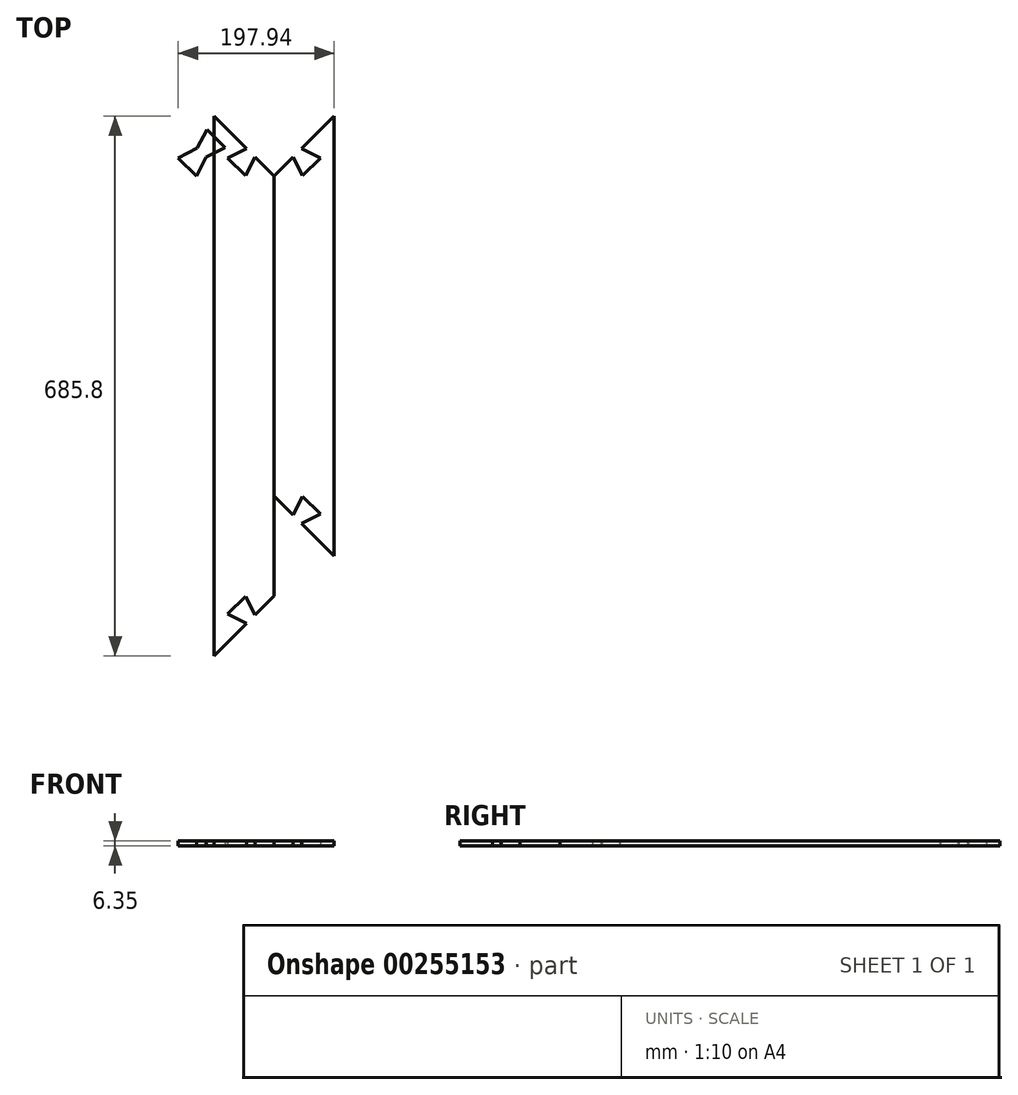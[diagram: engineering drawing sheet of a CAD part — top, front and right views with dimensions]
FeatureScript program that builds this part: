
annotation { "Feature Type Name" : "Feature", "Feature Type Description" : "" }
export const myFeature = defineFeature(function(context is Context, id is Id, definition is map)
    precondition{}
    {
        {
            assignVariable(context, id + "F0", {"name" : "BorderWidth", "anyValue" : 50});
        }
        {
            assignVariable(context, id + "F1", {"name" : "MaterialThickness", "anyValue" : 6.35});
        }
        {
            var Q0;
            Q0=qCreatedBy(makeId("Top.planeOp"),FACE);
            var sketch = newSketch(context, id + "F2", { "sketchPlane" : qUnion([Q0])});
            skLineSegment(sketch, "E0.bottom", {"start": v(203.2, 266.7) * mm, "end": v(-203.2, 266.7) * mm});
            skLineSegment(sketch, "E0.top", {"start": v(203.2, -266.7) * mm, "end": v(-203.2, -266.7) * mm});
            skLineSegment(sketch, "E0.left", {"start": v(203.2, 266.7) * mm, "end": v(203.2, -266.7) * mm});
            skLineSegment(sketch, "E0.right", {"start": v(-203.2, 266.7) * mm, "end": v(-203.2, -266.7) * mm});
            skPoint(sketch, "E0.middle", {"position": v(0, 0) * mm});
            skLineSegment(sketch, "E1.0", {"start": v(-279.4, 342.9) * mm, "end": v(-279.4, -342.9) * mm});
            skLineSegment(sketch, "E1.1", {"start": v(279.4, 342.9) * mm, "end": v(-279.4, 342.9) * mm});
            skLineSegment(sketch, "E1.2", {"start": v(279.4, 342.9) * mm, "end": v(279.4, -342.9) * mm});
            skLineSegment(sketch, "E1.3", {"start": v(279.4, -342.9) * mm, "end": v(-279.4, -342.9) * mm});
            skLineSegment(sketch, "E2", {"start": v(-203.2, 266.7) * mm, "end": v(-279.4, 342.9) * mm});
            skLineSegment(sketch, "E3", {"start": v(-238.22, 301.72) * mm, "end": v(-262.02, 289.6) * mm});
            skLineSegment(sketch, "E4", {"start": v(-262.02, 289.6) * mm, "end": v(-239.57, 267.15) * mm});
            skLineSegment(sketch, "E5", {"start": v(-239.57, 267.15) * mm, "end": v(-227.45, 290.95) * mm});
            skLineSegment(sketch, "E6", {"start": v(-227.45, 290.95) * mm, "end": v(-203.65, 303.07) * mm});
            skLineSegment(sketch, "E7", {"start": v(-203.65, 303.07) * mm, "end": v(-226.1, 325.52) * mm});
            skLineSegment(sketch, "E8", {"start": v(-226.1, 325.52) * mm, "end": v(-238.22, 301.72) * mm});
            skLineSegment(sketch, "E9.0", {"start": v(-262.44, 289.67) * mm, "end": v(-239.5, 266.73) * mm});
            skLineSegment(sketch, "E9.1", {"start": v(-227.26, 290.76) * mm, "end": v(-203.23, 303) * mm});
            skLineSegment(sketch, "E9.2", {"start": v(-203.23, 303) * mm, "end": v(-226.17, 325.94) * mm});
            skLineSegment(sketch, "E9.3", {"start": v(-239.5, 266.73) * mm, "end": v(-227.26, 290.76) * mm});
            skLineSegment(sketch, "E9.4", {"start": v(-226.17, 325.94) * mm, "end": v(-238.4, 301.9) * mm});
            skLineSegment(sketch, "E9.5", {"start": v(-238.4, 301.9) * mm, "end": v(-262.44, 289.67) * mm});
            skLineSegment(sketch, "E10", {"start": v(0, 342.9) * mm, "end": v(0, -342.9) * mm, "construction": true});
            skLineSegment(sketch, "E11", {"start": v(-279.4, 0) * mm, "end": v(279.4, 0) * mm, "construction": true});
            skLineSegment(sketch, "E12.MirrorCS", {"start": v(203.65, 303.07) * mm, "end": v(226.1, 325.52) * mm});
            skLineSegment(sketch, "E13.MirrorCS", {"start": v(262.44, 289.67) * mm, "end": v(239.5, 266.73) * mm});
            skLineSegment(sketch, "E14.MirrorCS", {"start": v(227.26, 290.76) * mm, "end": v(203.23, 303) * mm});
            skLineSegment(sketch, "E15.MirrorCS", {"start": v(239.5, 266.73) * mm, "end": v(227.26, 290.76) * mm});
            skLineSegment(sketch, "E16.MirrorCS", {"start": v(238.4, 301.9) * mm, "end": v(262.44, 289.67) * mm});
            skLineSegment(sketch, "E17.MirrorCS", {"start": v(227.45, 290.95) * mm, "end": v(203.65, 303.07) * mm});
            skLineSegment(sketch, "E18.MirrorCS", {"start": v(239.57, 267.15) * mm, "end": v(227.45, 290.95) * mm});
            skLineSegment(sketch, "E19.MirrorCS", {"start": v(262.02, 289.6) * mm, "end": v(239.57, 267.15) * mm});
            skLineSegment(sketch, "E20.MirrorCS", {"start": v(203.2, 266.7) * mm, "end": v(279.4, 342.9) * mm});
            skLineSegment(sketch, "E21.MirrorCS", {"start": v(226.1, 325.52) * mm, "end": v(238.22, 301.72) * mm});
            skLineSegment(sketch, "E22.MirrorCS", {"start": v(238.22, 301.72) * mm, "end": v(262.02, 289.6) * mm});
            skLineSegment(sketch, "E23.MirrorCS", {"start": v(203.23, 303) * mm, "end": v(226.17, 325.94) * mm});
            skLineSegment(sketch, "E24.MirrorCS", {"start": v(226.17, 325.94) * mm, "end": v(238.4, 301.9) * mm});
            skLineSegment(sketch, "E25.MirrorCS", {"start": v(-239.5, -266.73) * mm, "end": v(-227.26, -290.76) * mm});
            skLineSegment(sketch, "E26.MirrorCS", {"start": v(262.44, -289.67) * mm, "end": v(239.5, -266.73) * mm});
            skLineSegment(sketch, "E27.MirrorCS", {"start": v(203.65, -303.07) * mm, "end": v(226.1, -325.52) * mm});
            skLineSegment(sketch, "E28.MirrorCS", {"start": v(239.5, -266.73) * mm, "end": v(227.26, -290.76) * mm});
            skLineSegment(sketch, "E29.MirrorCS", {"start": v(-227.45, -290.95) * mm, "end": v(-203.65, -303.07) * mm});
            skLineSegment(sketch, "E30.MirrorCS", {"start": v(-239.57, -267.15) * mm, "end": v(-227.45, -290.95) * mm});
            skLineSegment(sketch, "E31.MirrorCS", {"start": v(-203.65, -303.07) * mm, "end": v(-226.1, -325.52) * mm});
            skLineSegment(sketch, "E32.MirrorCS", {"start": v(203.23, -303) * mm, "end": v(226.17, -325.94) * mm});
            skLineSegment(sketch, "E33.MirrorCS", {"start": v(203.2, -266.7) * mm, "end": v(279.4, -342.9) * mm});
            skLineSegment(sketch, "E34.MirrorCS", {"start": v(227.26, -290.76) * mm, "end": v(203.23, -303) * mm});
            skLineSegment(sketch, "E35.MirrorCS", {"start": v(238.22, -301.72) * mm, "end": v(262.02, -289.6) * mm});
            skLineSegment(sketch, "E36.MirrorCS", {"start": v(-203.23, -303) * mm, "end": v(-226.17, -325.94) * mm});
            skLineSegment(sketch, "E37.MirrorCS", {"start": v(262.02, -289.6) * mm, "end": v(239.57, -267.15) * mm});
            skLineSegment(sketch, "E38.MirrorCS", {"start": v(227.45, -290.95) * mm, "end": v(203.65, -303.07) * mm});
            skLineSegment(sketch, "E39.MirrorCS", {"start": v(226.17, -325.94) * mm, "end": v(238.4, -301.9) * mm});
            skLineSegment(sketch, "E40.MirrorCS", {"start": v(-226.17, -325.94) * mm, "end": v(-238.4, -301.9) * mm});
            skLineSegment(sketch, "E41.MirrorCS", {"start": v(226.1, -325.52) * mm, "end": v(238.22, -301.72) * mm});
            skLineSegment(sketch, "E42.MirrorCS", {"start": v(-203.2, -266.7) * mm, "end": v(-279.4, -342.9) * mm});
            skLineSegment(sketch, "E43.MirrorCS", {"start": v(-227.26, -290.76) * mm, "end": v(-203.23, -303) * mm});
            skLineSegment(sketch, "E44.MirrorCS", {"start": v(-238.4, -301.9) * mm, "end": v(-262.44, -289.67) * mm});
            skLineSegment(sketch, "E45.MirrorCS", {"start": v(239.57, -267.15) * mm, "end": v(227.45, -290.95) * mm});
            skLineSegment(sketch, "E46.MirrorCS", {"start": v(-262.02, -289.6) * mm, "end": v(-239.57, -267.15) * mm});
            skLineSegment(sketch, "E47.MirrorCS", {"start": v(-226.1, -325.52) * mm, "end": v(-238.22, -301.72) * mm});
            skLineSegment(sketch, "E48.MirrorCS", {"start": v(238.4, -301.9) * mm, "end": v(262.44, -289.67) * mm});
            skLineSegment(sketch, "E49.MirrorCS", {"start": v(-262.44, -289.67) * mm, "end": v(-239.5, -266.73) * mm});
            skLineSegment(sketch, "E50.MirrorCS", {"start": v(-238.22, -301.72) * mm, "end": v(-262.02, -289.6) * mm});
            skSolve(sketch);
        }
        {
            var Q0;
            {var subQ0=sQuery(id+"F2.wireOp",EDGE,"E3");Q0=makeQuery(id+"F2.imprint","IMPRINT",FACE,{"disambiguationData":[TD([[makeQuery(id+"F2.imprint","IMPRINT",EDGE,{"derivedFrom":subQ0}),1.0]])]});}
            var Q1;
            {var subQ0=sQuery(id+"F2.wireOp",EDGE,"E3");Q1=makeQuery(id+"F2.imprint","IMPRINT",FACE,{"disambiguationData":[TD([[makeQuery(id+"F2.imprint","IMPRINT",EDGE,{"derivedFrom":subQ0}),-1.0]])]});}
            var Q2;
            {var subQ2=sQuery(id+"F2.wireOp",EDGE,"E6");Q2=makeQuery(id+"F2.imprint","IMPRINT",FACE,{"disambiguationData":[TD([[makeQuery(id+"F2.imprint","IMPRINT",EDGE,{"derivedFrom":subQ2}),1.0]])]});}
            var Q3;
            {var subQ0=sQuery(id+"F2.wireOp",EDGE,"E6");Q3=makeQuery(id+"F2.imprint","IMPRINT",FACE,{"disambiguationData":[TD([[makeQuery(id+"F2.imprint","IMPRINT",EDGE,{"derivedFrom":subQ0}),-1.0]])]});}
            extrude(context, id + "F3", {"entities" : qUnion([Q0, Q1, Q2, Q3]), "depth" : (getVariable(context, 'MaterialThickness')) * mm});
        }
        {
            var Q0;
            Q0=makeQuery(id+"F3.opExtrude","SWEPT_BODY",BODY,{"disambiguationData":[OSD([sQuery(id+"F2.wireOp",EDGE,"E9.0"),sQuery(id+"F2.wireOp",EDGE,"E9.1"),sQuery(id+"F2.wireOp",EDGE,"E9.2"),sQuery(id+"F2.wireOp",EDGE,"E9.3"),sQuery(id+"F2.wireOp",EDGE,"E9.4"),sQuery(id+"F2.wireOp",EDGE,"E9.5")])]});
            transform(context, id + "F4", {"entities" : qUnion([Q0]), "transformType" : TransformType.TRANSLATION_3D, "dx" : (-getVariable(context, 'BorderWidth') * 1.25) * mm, "dy" : 0 * mm, "dz" : 0 * mm, "makeCopy" : false});
        }
        {
            var Q0;
            {var subQ1=sQuery(id+"F2.wireOp",EDGE,"E0.right");Q0=makeQuery(id+"F2.imprint","IMPRINT",FACE,{"disambiguationData":[TD([[makeQuery(id+"F2.imprint","IMPRINT",EDGE,{"derivedFrom":subQ1}),-1.0]])]});}
            var Q1;
            {var subQ0=sQuery(id+"F2.wireOp",EDGE,"E3");Q1=makeQuery(id+"F2.imprint","IMPRINT",FACE,{"disambiguationData":[TD([[makeQuery(id+"F2.imprint","IMPRINT",EDGE,{"derivedFrom":subQ0}),-1.0]])]});}
            var Q2;
            {var subQ3=sQuery(id+"F2.wireOp",EDGE,"E25.MirrorCS");Q2=makeQuery(id+"F2.imprint","IMPRINT",FACE,{"disambiguationData":[TD([[makeQuery(id+"F2.imprint","IMPRINT",EDGE,{"derivedFrom":subQ3}),-1.0]])]});}
            extrude(context, id + "F5", {"entities" : qUnion([Q0, Q1, Q2]), "depth" : (getVariable(context, 'MaterialThickness')) * mm});
        }
        {
            var Q0;
            {var subQ3=sQuery(id+"F2.wireOp",EDGE,"E0.bottom");Q0=makeQuery(id+"F2.imprint","IMPRINT",FACE,{"disambiguationData":[TD([[makeQuery(id+"F2.imprint","IMPRINT",EDGE,{"derivedFrom":subQ3}),-1.0]])]});}
            var Q1;
            {var subQ0=sQuery(id+"F2.wireOp",EDGE,"E6");Q1=makeQuery(id+"F2.imprint","IMPRINT",FACE,{"disambiguationData":[TD([[makeQuery(id+"F2.imprint","IMPRINT",EDGE,{"derivedFrom":subQ0}),-1.0]])]});}
            var Q2;
            Q2=makeQuery(id+"F2.imprint","IMPRINT",FACE,{"disambiguationData":[TD([[makeQuery(id+"F2.imprint","IMPRINT",EDGE,{"derivedFrom":sQuery(id+"F2.wireOp",EDGE,"E12.MirrorCS")}),1.0]])]});
            extrude(context, id + "F6", {"entities" : qUnion([Q0, Q1, Q2]), "depth" : (getVariable(context, 'MaterialThickness')) * mm});
        }
        {
            var Q0;
            Q0=makeQuery(id+"F6.opExtrude","SWEPT_BODY",BODY,{"disambiguationData":[OSD([sQuery(id+"F2.wireOp",EDGE,"E0.bottom"),sQuery(id+"F2.wireOp",EDGE,"E1.1"),sQuery(id+"F2.wireOp",EDGE,"E2"),sQuery(id+"F2.wireOp",EDGE,"E6"),sQuery(id+"F2.wireOp",EDGE,"E7"),sQuery(id+"F2.wireOp",EDGE,"E8"),sQuery(id+"F2.wireOp",EDGE,"E12.MirrorCS"),sQuery(id+"F2.wireOp",EDGE,"E17.MirrorCS"),sQuery(id+"F2.wireOp",EDGE,"E20.MirrorCS"),sQuery(id+"F2.wireOp",EDGE,"E21.MirrorCS")])]});
            var Q1;
            Q1=makeQuery(id+"F5.opExtrude","SWEPT_EDGE",EDGE,{"disambiguationData":[OSD([sQuery(id+"F2.wireOp",EDGE,"E0.bottom"),sQuery(id+"F2.wireOp",EDGE,"E0.right"),sQuery(id+"F2.wireOp",EDGE,"E2")])]});
            transform(context, id + "F7", {"entities" : qUnion([Q0]), "transformType" : TransformType.ROTATION, "transformAxis" : qUnion([Q1]), "angle" : 90 * degree, "makeCopy" : false});
        }
    });
